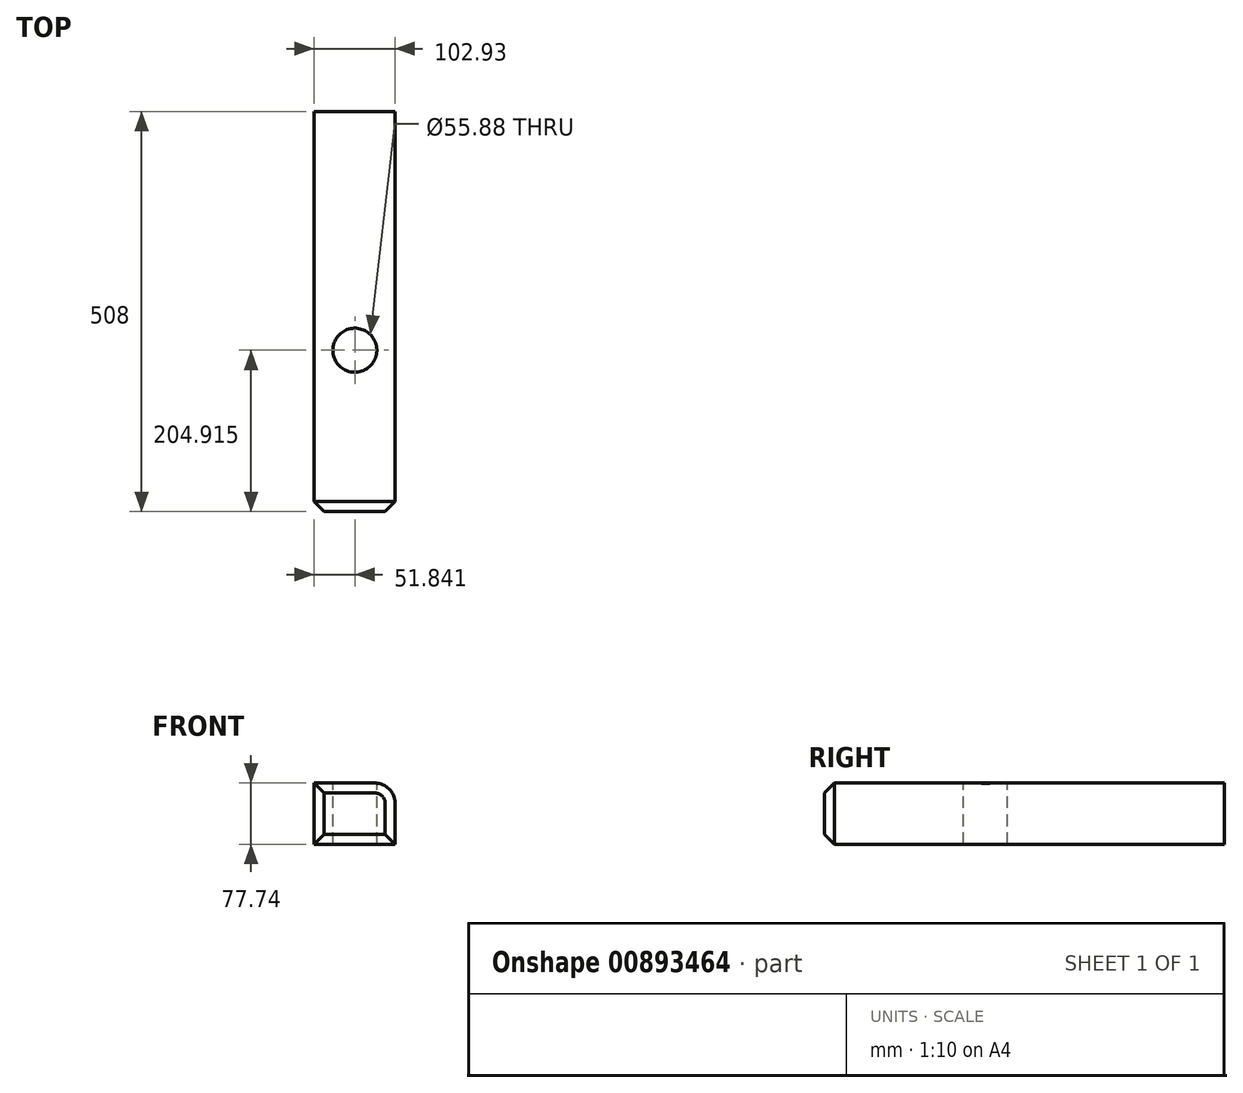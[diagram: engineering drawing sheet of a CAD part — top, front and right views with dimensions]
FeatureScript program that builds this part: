
annotation { "Feature Type Name" : "Feature", "Feature Type Description" : "" }
export const myFeature = defineFeature(function(context is Context, id is Id, definition is map)
    precondition{}
    {
        {
            var Q0;
            Q0=qCreatedBy(makeId("Front.planeOp"),FACE);
            var sketch = newSketch(context, id + "F0", { "sketchPlane" : qUnion([Q0])});
            skLineSegment(sketch, "E0.bottom", {"start": v(-78.29, 49.45) * mm, "end": v(24.64, 49.45) * mm});
            skLineSegment(sketch, "E0.top", {"start": v(-78.29, -28.29) * mm, "end": v(24.64, -28.29) * mm});
            skLineSegment(sketch, "E0.left", {"start": v(-78.29, 49.45) * mm, "end": v(-78.29, -28.29) * mm});
            skLineSegment(sketch, "E0.right", {"start": v(24.64, 49.45) * mm, "end": v(24.64, -28.29) * mm});
            skSolve(sketch);
        }
        {
            var Q0;
            Q0=makeQuery(id+"F0.imprint","IMPRINT",FACE,{"disambiguationData":[TD([[makeQuery(id+"F0.imprint","IMPRINT",EDGE,{"derivedFrom":sQuery(id+"F0.wireOp",EDGE,"E0.bottom")}),-1.0]])]});
            extrude(context, id + "F1", {"entities" : qUnion([Q0]), "depth" : 508 * mm, "offsetDistance" : 25.4 * mm});
        }
        {
            var Q0;
            Q0=makeQuery(id+"F1.opExtrude","SWEPT_EDGE",EDGE,{"disambiguationData":[OSD([sQuery(id+"F0.wireOp",EDGE,"E0.bottom"),sQuery(id+"F0.wireOp",EDGE,"E0.right")])]});
            fillet(context, id + "F2", {"entities" : qUnion([Q0]), "radius" : 25.4 * mm, "tangentPropagation" : true, "allowEdgeOverflow" : false});
        }
        {
            var Q0;
            Q0=makeQuery(id+"F1.opExtrude","SWEPT_FACE",FACE,{"disambiguationData":[OSD([sQuery(id+"F0.wireOp",EDGE,"E0.bottom")])]});
            var sketch = newSketch(context, id + "F3", { "sketchPlane" : qUnion([Q0])});
            skCircle(sketch, "E1", {"center": v(-26.45, -303.08) * mm, "radius": 36.28 * mm});
            skSolve(sketch);
        }
        {
            var Q0;
            Q0=sQuery(id+"F3.wireOp",VERTEX,"E1.center");
            var Q1;
            Q1=makeQuery(id+"F1.opExtrude","SWEPT_BODY",BODY,{"disambiguationData":[OSD([sQuery(id+"F0.wireOp",EDGE,"E0.bottom"),sQuery(id+"F0.wireOp",EDGE,"E0.top"),sQuery(id+"F0.wireOp",EDGE,"E0.left"),sQuery(id+"F0.wireOp",EDGE,"E0.right")])]});
            hole(context, id + "F4", {"style" : HoleStyle.SIMPLE, "endStyle" : HoleEndStyle.THROUGH, "holeDiameter" : 55.88 * mm, "majorDiameter" : 6.35 * mm, "isTappedThrough" : true, "tappedDepth" : 12.7 * mm, "tapClearance" : 3, "locations" : qUnion([Q0]), "scope" : qUnion([Q1])});
        }
        {
            var Q0;
            Q0=makeQuery(id+"F1.opExtrude","CAP_FACE",FACE,{"disambiguationData":[OSD([sQuery(id+"F0.wireOp",EDGE,"E0.bottom"),sQuery(id+"F0.wireOp",EDGE,"E0.top"),sQuery(id+"F0.wireOp",EDGE,"E0.left"),sQuery(id+"F0.wireOp",EDGE,"E0.right")])],"isStart":false});
            chamfer(context, id + "F5", {"entities" : qUnion([Q0]), "width" : 12.7 * mm, "tangentPropagation" : true});
        }
    });
